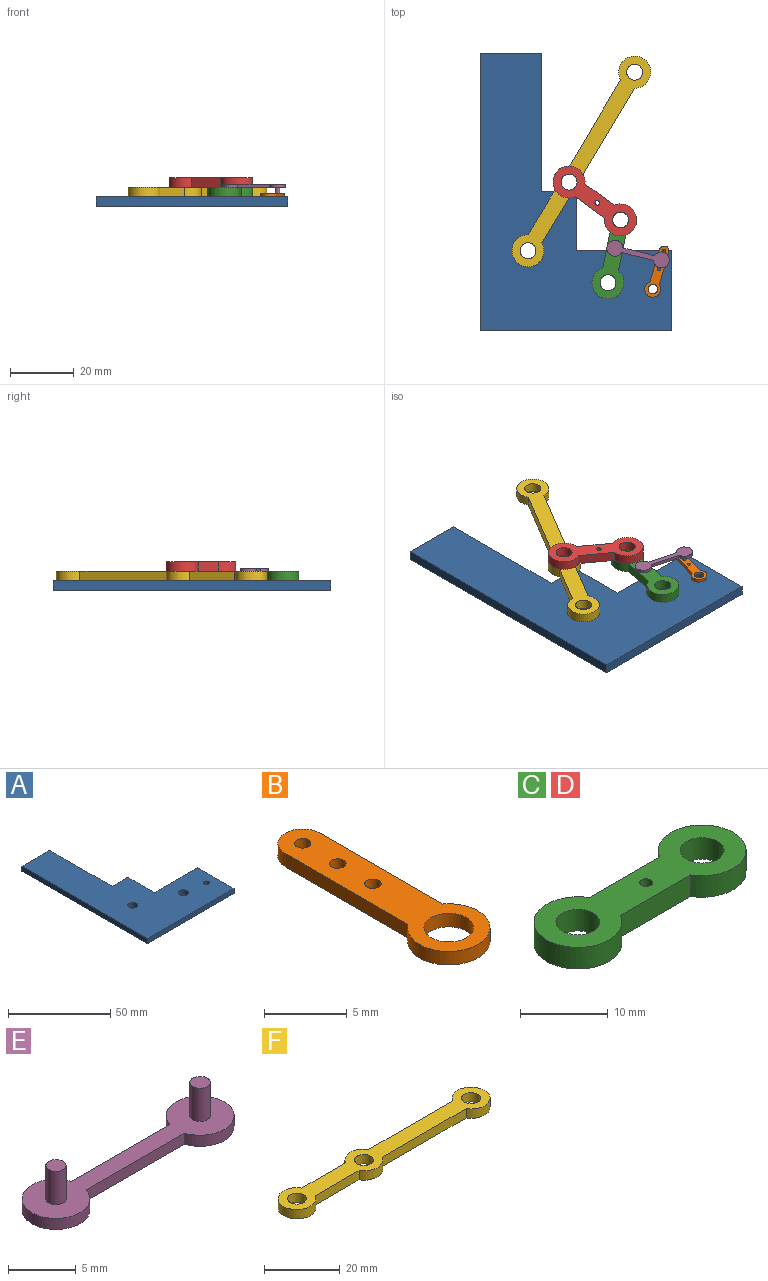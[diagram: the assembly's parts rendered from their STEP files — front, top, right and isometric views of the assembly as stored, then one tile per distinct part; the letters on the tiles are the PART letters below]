
ASSEMBLY  parts=6 mates=7
PART A: 13 faces, bbox 60x86.7x3 mm
  f0: plane 10.88x3mm, normal (0,1,0), area 32.6mm2, adj f1,f8,f11,f12
  f1: plane 43.28x3mm, normal (1,0,0), area 129.9mm2, adj f0,f2,f11,f12
  f2: plane 19.12x3mm, normal (0,1,0), area 57.4mm2, adj f1,f3,f11,f12
  f3: plane 86.73x3mm, normal (-1,0,0), area 260.2mm2, adj f2,f4,f11,f12
  f4: plane 60x3mm, normal (0,-1,0), area 180mm2, adj f3,f5,f11,f12
  f5: plane 25x3mm, normal (1,0,0), area 75mm2, adj f4,f6,f11,f12
  f6: plane 30x3mm, normal (0,1,0), area 90mm2, adj f5,f8,f11,f12
  f7: cylinder r=1.5mm len=3mm, axis (0,0,-1), area 28.3mm2, adj f11,f12
  f8: plane 18.44x3mm, normal (1,0,0), area 55.3mm2, adj f0,f6,f11,f12
  f9: cylinder r=2.5mm len=5mm, axis (0,0,-1), area 47.1mm2, adj f11,f12
  f10: cylinder r=2.5mm len=5mm, axis (0,0,-1), area 47.1mm2, adj f11,f12
  f11: plane 86.73x60mm, normal (0,0,1), area 2834.6mm2, adj f0,f1,f2,f3,f4,f5,f6,f7
  f12: plane 86.73x60mm, normal (0,0,-1), area 2834.6mm2, adj f0,f1,f2,f3,f4,f5,f6,f7
PART B: 10 faces, bbox 5x16.5x1 mm
  f0: plane 10.5x1mm, normal (-1,0,0), area 10.5mm2, adj f1,f5,f8,f9
  f1: cylinder r=2.5mm len=5mm, axis (0,0,-1), area 12.5mm2, adj f0,f2,f8,f9
  f2: plane 10.5x1mm, normal (1,0,0), area 10.5mm2, adj f1,f5,f8,f9
  f3: cylinder r=0.5mm len=1mm, axis (0,0,-1), area 3.1mm2, adj f8,f9
  f4: cylinder r=0.5mm len=1mm, axis (0,0,-1), area 3.1mm2, adj f8,f9
  f5: cylinder r=1.5mm len=3mm, axis (0,0,-1), area 4.7mm2, adj f0,f2,f8,f9
  f6: cylinder r=1.5mm len=3mm, axis (0,0,-1), area 9.4mm2, adj f8,f9
  f7: cylinder r=0.5mm len=1mm, axis (0,0,-1), area 3.1mm2, adj f8,f9
  f8: plane 16.5x5mm, normal (0,0,1), area 44.2mm2, adj f0,f1,f2,f3,f4,f5,f6,f7
  f9: plane 16.5x5mm, normal (0,0,-1), area 44.2mm2, adj f0,f1,f2,f3,f4,f5,f6,f7
PART C: 9 faces, bbox 30x10x3 mm
  f0: plane 11.34x3mm, normal (0,1,0), area 34mm2, adj f1,f5,f7,f8
  f1: cylinder r=5mm len=10mm, axis (0,0,-1), area 78.5mm2, adj f0,f2,f7,f8
  f2: plane 11.34x3mm, normal (0,-1,0), area 34mm2, adj f1,f5,f7,f8
  f3: cylinder r=0.75mm len=3mm, axis (0,0,-1), area 14.1mm2, adj f7,f8
  f4: cylinder r=2.5mm len=5mm, axis (0,0,-1), area 47.1mm2, adj f7,f8
  f5: cylinder r=5mm len=10mm, axis (0,0,-1), area 78.5mm2, adj f0,f2,f7,f8
  f6: cylinder r=2.5mm len=5mm, axis (0,0,-1), area 47.1mm2, adj f7,f8
  f7: plane 30x10mm, normal (0,0,1), area 168.2mm2, adj f0,f1,f2,f3,f4,f5,f6
  f8: plane 30x10mm, normal (0,0,-1), area 168.2mm2, adj f0,f1,f2,f3,f4,f5,f6
PART D: same geometry as C
PART E: 10 faces, bbox 20x5x4 mm
  f0: cylinder r=2.5mm len=5mm, axis (0,0,-1), area 14.2mm2, adj f1,f3,f4,f5
  f1: plane 10.23x1mm, normal (0,-1,0), area 10.2mm2, adj f0,f2,f4,f5
  f2: cylinder r=2.5mm len=5mm, axis (0,0,-1), area 14.2mm2, adj f1,f3,f4,f5
  f3: plane 10.23x1mm, normal (0,1,0), area 10.2mm2, adj f0,f2,f4,f5
  f4: plane 20x5mm, normal (0,0,1), area 50.8mm2, adj f0,f1,f2,f3,f6,f8
  f5: plane 20x5mm, normal (0,0,-1), area 54.4mm2, adj f0,f1,f2,f3
  f6: cylinder r=0.75mm len=3mm, axis (0,0,-1), area 14.1mm2, adj f4,f7
  f7: plane 1.5x1.5mm, normal (0,0,1), area 1.8mm2, adj f6
  f8: cylinder r=0.75mm len=3mm, axis (0,0,-1), area 14.1mm2, adj f4,f9
  f9: plane 1.5x1.5mm, normal (0,0,1), area 1.8mm2, adj f8
PART F: 13 faces, bbox 75x10x3 mm
  f0: plane 16.34x3mm, normal (0,1,0), area 49mm2, adj f1,f9,f11,f12
  f1: cylinder r=5mm len=10mm, axis (0,0,-1), area 78.5mm2, adj f0,f2,f11,f12
  f2: plane 16.34x3mm, normal (0,-1,0), area 49mm2, adj f1,f3,f11,f12
  f3: cylinder r=5mm len=8.66mm, axis (0,0,-1), area 31.4mm2, adj f2,f4,f11,f12
  f4: plane 31.34x3mm, normal (0,-1,0), area 94mm2, adj f3,f5,f11,f12
  f5: cylinder r=5mm len=10mm, axis (0,0,-1), area 78.5mm2, adj f4,f6,f11,f12
  f6: plane 31.34x3mm, normal (0,1,0), area 94mm2, adj f5,f9,f11,f12
  f7: cylinder r=2.5mm len=5mm, axis (0,0,-1), area 47.1mm2, adj f11,f12
  f8: cylinder r=2.5mm len=5mm, axis (0,0,-1), area 47.1mm2, adj f11,f12
  f9: cylinder r=5mm len=8.66mm, axis (0,0,-1), area 31.4mm2, adj f0,f6,f11,f12
  f10: cylinder r=2.5mm len=5mm, axis (0,0,-1), area 47.1mm2, adj f11,f12
  f11: plane 75x10mm, normal (0,0,1), area 406.1mm2, adj f0,f1,f2,f3,f4,f5,f6,f7
  f12: plane 75x10mm, normal (0,0,-1), area 406.1mm2, adj f0,f1,f2,f3,f4,f5,f6,f7
PLACE A t=(-10,0,0)mm
PLACE B rot(axis=(0,0,-1),16.5deg) t=(14,-2,3)mm
PLACE C rot(axis=(0,0,1),78.7deg) t=(0,0,3)mm
PLACE D rot(axis=(0.95,-0.31,0),180deg) t=(-12.18,31.46,9)mm
PLACE E rot(axis=(0.99,-0.12,0),180deg) t=(16.7,7.11,7)mm
PLACE F rot(axis=(0,0,1),59.1deg) t=(-12.18,31.46,3)mm
MATE revolute E.f8 <-> C.f3  axis (0,0,-1) through (2.16,10.79,3)mm
MATE revolute E.f6 <-> B.f4  axis (0,0,1) through (16.7,7.11,3)mm
MATE revolute D.f1 <-> F.f7  axis (0,0,-1) through (-12.18,31.46,6)mm
MATE revolute B.f6 <-> A.f7  axis (0,0,-1) through (14,-2,3)mm
MATE revolute C.f4 <-> A.f10  axis (0,0,-1) through (0,0,3)mm
MATE revolute D.f6 <-> C.f6  axis (0,0,-1) through (3.93,19.61,6)mm
MATE revolute F.f8 <-> A.f9  axis (0,0,-1) through (-25,10,3)mm
